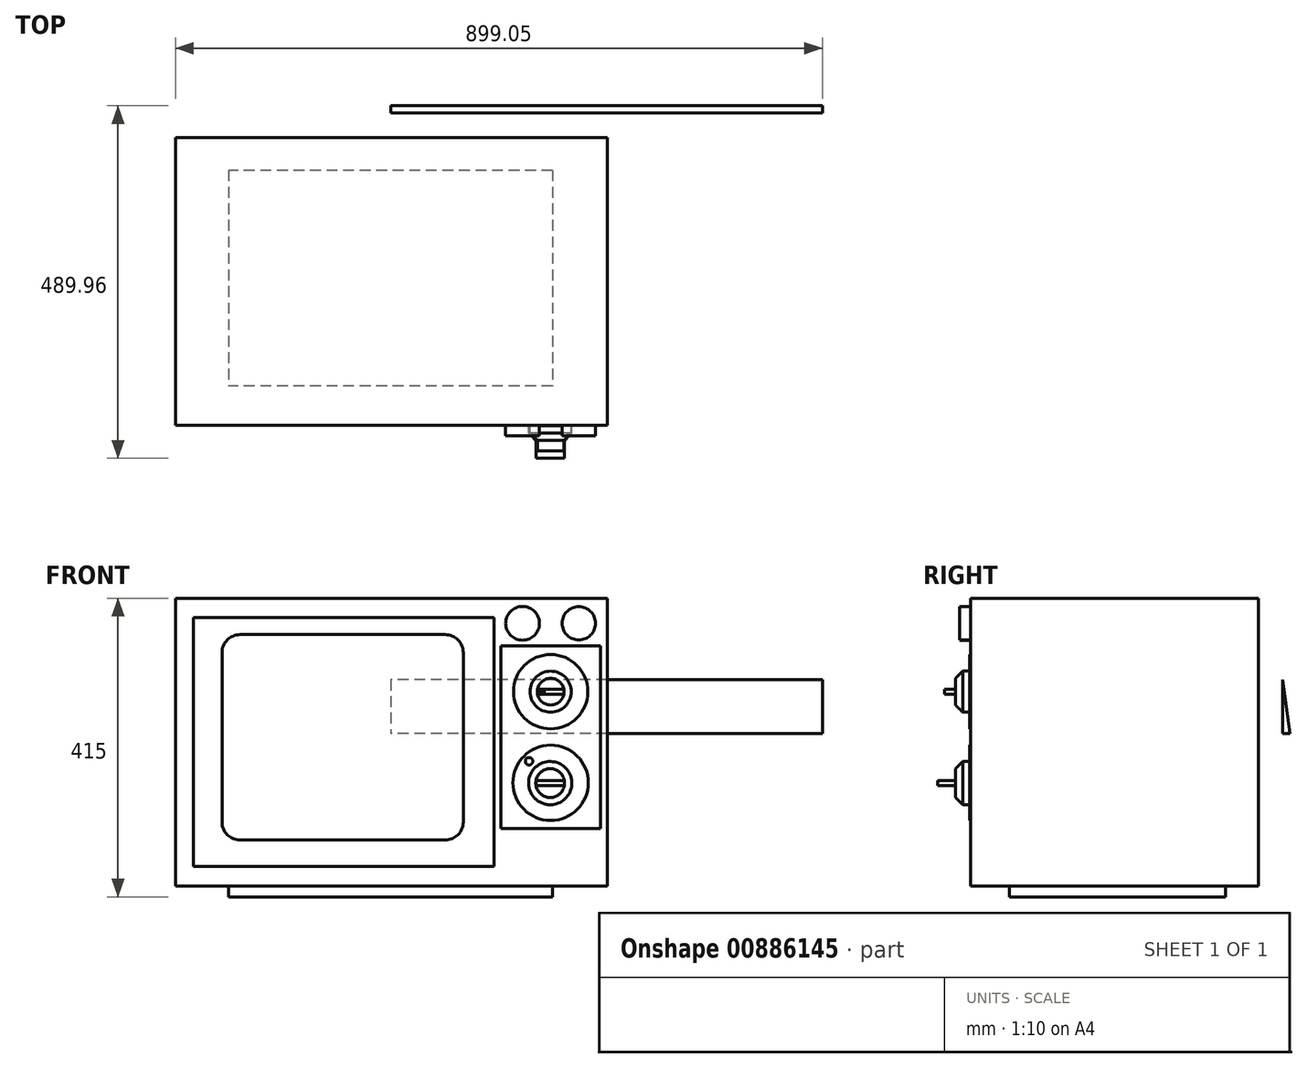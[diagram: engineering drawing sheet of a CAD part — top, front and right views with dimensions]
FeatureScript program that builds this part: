
annotation { "Feature Type Name" : "Feature", "Feature Type Description" : "" }
export const myFeature = defineFeature(function(context is Context, id is Id, definition is map)
    precondition{}
    {
        {
            var Q0;
            Q0=qCreatedBy(makeId("Front.planeOp"),FACE);
            var sketch = newSketch(context, id + "F0", { "sketchPlane" : qUnion([Q0])});
            skLineSegment(sketch, "E0.bottom", {"start": v(-299.05, 194.51) * mm, "end": v(300.95, 194.51) * mm});
            skLineSegment(sketch, "E0.top", {"start": v(-299.05, -205.49) * mm, "end": v(300.95, -205.49) * mm});
            skLineSegment(sketch, "E0.left", {"start": v(-299.05, 194.51) * mm, "end": v(-299.05, -205.49) * mm});
            skLineSegment(sketch, "E0.right", {"start": v(300.95, 194.51) * mm, "end": v(300.95, -205.49) * mm});
            skSolve(sketch);
        }
        {
            var Q0;
            Q0=makeQuery(id+"F0.imprint","IMPRINT",FACE,{"disambiguationData":[TD([[makeQuery(id+"F0.imprint","IMPRINT",EDGE,{"derivedFrom":sQuery(id+"F0.wireOp",EDGE,"E0.bottom")}),-1.0]])]});
            extrude(context, id + "F1", {"entities" : qUnion([Q0]), "depth" : 400 * mm, "offsetDistance" : 25 * mm});
        }
        {
            var Q0;
            Q0=makeQuery(id+"F1.opExtrude","CAP_FACE",FACE,{"disambiguationData":[OSD([sQuery(id+"F0.wireOp",EDGE,"E0.bottom"),sQuery(id+"F0.wireOp",EDGE,"E0.top"),sQuery(id+"F0.wireOp",EDGE,"E0.left"),sQuery(id+"F0.wireOp",EDGE,"E0.right")])],"isStart":false});
            var sketch = newSketch(context, id + "F2", { "sketchPlane" : qUnion([Q0])});
            skLineSegment(sketch, "E1.bottom", {"start": v(-274.22, 167.93) * mm, "end": v(144, 167.93) * mm});
            skLineSegment(sketch, "E1.top", {"start": v(-274.22, -178.07) * mm, "end": v(144, -178.07) * mm});
            skLineSegment(sketch, "E1.left", {"start": v(-274.22, 167.93) * mm, "end": v(-274.22, -178.07) * mm});
            skLineSegment(sketch, "E1.right", {"start": v(144, 167.93) * mm, "end": v(144, -178.07) * mm});
            skSolve(sketch);
        }
        {
            var Q0;
            Q0=makeQuery(id+"F2.imprint","IMPRINT",FACE,{"disambiguationData":[TD([[makeQuery(id+"F2.imprint","IMPRINT",EDGE,{"derivedFrom":sQuery(id+"F2.wireOp",EDGE,"E1.bottom")}),-1.0]])]});
            var sketch = newSketch(context, id + "F3", { "sketchPlane" : qUnion([Q0])});
            skSolve(sketch);
        }
        {
            var Q0;
            Q0=makeQuery(id+"F3.imprint","IMPRINT",FACE,{"disambiguationData":[TD([[makeQuery(id+"F3.imprint","IMPRINT",EDGE,{"derivedFrom":makeQuery(id+"F2.imprint","IMPRINT",EDGE,{"derivedFrom":sQuery(id+"F2.wireOp",EDGE,"E1.bottom")})}),-1.0]])]});
            extrude(context, id + "F4", {"entities" : qUnion([Q0]), "depth" : 0.01 * mm, "offsetDistance" : 25 * mm});
        }
        {
            var Q0;
            Q0=makeQuery(id+"F4.opExtrude","CAP_FACE",FACE,{"disambiguationData":[OSD([sQuery(id+"F2.wireOp",EDGE,"E1.bottom"),sQuery(id+"F2.wireOp",EDGE,"E1.top"),sQuery(id+"F2.wireOp",EDGE,"E1.left"),sQuery(id+"F2.wireOp",EDGE,"E1.right")])],"isStart":false});
            fillet(context, id + "F5", {"entities" : qUnion([Q0]), "radius" : 25 * mm, "tangentPropagation" : true, "allowEdgeOverflow" : false});
        }
        {
            var Q0;
            Q0=makeQuery(id+"F4.opExtrude","CAP_FACE",FACE,{"disambiguationData":[OSD([sQuery(id+"F2.wireOp",EDGE,"E1.bottom"),sQuery(id+"F2.wireOp",EDGE,"E1.top"),sQuery(id+"F2.wireOp",EDGE,"E1.left"),sQuery(id+"F2.wireOp",EDGE,"E1.right")])],"isStart":false});
            var sketch = newSketch(context, id + "F6", { "sketchPlane" : qUnion([Q0])});
            skLineSegment(sketch, "E2.bottom", {"start": v(-209.34, 144.13) * mm, "end": v(75.88, 144.13) * mm});
            skLineSegment(sketch, "E2.top", {"start": v(-209.34, -141.42) * mm, "end": v(75.88, -141.42) * mm});
            skLineSegment(sketch, "E2.left", {"start": v(-234.34, 119.13) * mm, "end": v(-234.34, -116.42) * mm});
            skLineSegment(sketch, "E2.right", {"start": v(100.88, 119.13) * mm, "end": v(100.88, -116.42) * mm});
            skPoint(sketch, "E3.visualSharp", {"position": v(-234.34, 144.13) * mm});
            skArc(sketch, "E3.filletArc", {"start": v(-209.34, 144.13) * mm, "mid": v(-227.02, 136.8) * mm, "end": v(-234.34, 119.13) * mm});
            skPoint(sketch, "E4.visualSharp", {"position": v(100.88, 144.13) * mm});
            skArc(sketch, "E4.filletArc", {"start": v(100.88, 119.13) * mm, "mid": v(93.55, 136.8) * mm, "end": v(75.88, 144.13) * mm});
            skPoint(sketch, "E5.visualSharp", {"position": v(100.88, -141.42) * mm});
            skArc(sketch, "E5.filletArc", {"start": v(75.88, -141.42) * mm, "mid": v(93.55, -134.1) * mm, "end": v(100.88, -116.42) * mm});
            skPoint(sketch, "E6.visualSharp", {"position": v(-234.34, -141.42) * mm});
            skArc(sketch, "E6.filletArc", {"start": v(-234.34, -116.42) * mm, "mid": v(-227.02, -134.1) * mm, "end": v(-209.34, -141.42) * mm});
            skSolve(sketch);
        }
        {
            var Q0;
            Q0=makeQuery(id+"F6.imprint","IMPRINT",FACE,{"disambiguationData":[TD([[makeQuery(id+"F6.imprint","IMPRINT",EDGE,{"derivedFrom":sQuery(id+"F6.wireOp",EDGE,"E2.bottom")}),-1.0]])]});
            extrude(context, id + "F7", {"entities" : qUnion([Q0]), "depth" : 0.01 * mm, "offsetDistance" : 25 * mm});
        }
        {
            var Q0;
            Q0=makeQuery(id+"F2.imprint","IMPRINT",FACE,{"disambiguationData":[TD([[makeQuery(id+"F2.imprint","IMPRINT",EDGE,{"derivedFrom":sQuery(id+"F2.wireOp",EDGE,"E1.bottom")}),1.0]])]});
            var sketch = newSketch(context, id + "F8", { "sketchPlane" : qUnion([Q0])});
            skCircle(sketch, "E7", {"center": v(183.33, 159.85) * mm, "radius": 23.48 * mm});
            skCircle(sketch, "E8", {"center": v(261.48, 159.85) * mm, "radius": 23.15 * mm});
            skSolve(sketch);
        }
        {
            var Q0;
            Q0 = qSketchRegion(id + "F8", true);
            extrude(context, id + "F9", {"entities" : qUnion([Q0]), "depth" : 15 * mm, "offsetDistance" : 25 * mm});
        }
        {
            var Q0;
            Q0=makeQuery(id+"F2.imprint","IMPRINT",FACE,{"disambiguationData":[TD([[makeQuery(id+"F2.imprint","IMPRINT",EDGE,{"derivedFrom":sQuery(id+"F2.wireOp",EDGE,"E1.bottom")}),1.0]])]});
            var sketch = newSketch(context, id + "F10", { "sketchPlane" : qUnion([Q0])});
            skLineSegment(sketch, "E9.bottom", {"start": v(153.12, 128.25) * mm, "end": v(291.63, 128.25) * mm});
            skLineSegment(sketch, "E9.top", {"start": v(153.12, -125.33) * mm, "end": v(291.63, -125.33) * mm});
            skLineSegment(sketch, "E9.left", {"start": v(153.12, 128.25) * mm, "end": v(153.12, -125.33) * mm});
            skLineSegment(sketch, "E9.right", {"start": v(291.63, 128.25) * mm, "end": v(291.63, -125.33) * mm});
            skSolve(sketch);
        }
        {
            var Q0;
            Q0 = qSketchRegion(id + "F10", true);
            extrude(context, id + "F11", {"entities" : qUnion([Q0]), "depth" : 0.01 * mm, "offsetDistance" : 25 * mm});
        }
        {
            var Q0;
            Q0=makeQuery(id+"F11.opExtrude","CAP_FACE",FACE,{"disambiguationData":[OSD([sQuery(id+"F10.wireOp",EDGE,"E9.bottom"),sQuery(id+"F10.wireOp",EDGE,"E9.top"),sQuery(id+"F10.wireOp",EDGE,"E9.left"),sQuery(id+"F10.wireOp",EDGE,"E9.right")])],"isStart":false});
            var sketch = newSketch(context, id + "F12", { "sketchPlane" : qUnion([Q0])});
            skCircle(sketch, "E10", {"center": v(222.37, 64.86) * mm, "radius": 51.65 * mm});
            skCircle(sketch, "E11", {"center": v(222.37, -61.94) * mm, "radius": 52.4 * mm});
            skSolve(sketch);
        }
        {
            var Q0;
            Q0=makeQuery(id+"F12.imprint","IMPRINT",FACE,{"disambiguationData":[TD([[makeQuery(id+"F12.imprint","IMPRINT",EDGE,{"derivedFrom":sQuery(id+"F12.wireOp",EDGE,"E10")}),1.0]])]});
            var Q1;
            Q1=makeQuery(id+"F12.imprint","IMPRINT",FACE,{"disambiguationData":[TD([[makeQuery(id+"F12.imprint","IMPRINT",EDGE,{"derivedFrom":sQuery(id+"F12.wireOp",EDGE,"E11")}),1.0]])]});
            extrude(context, id + "F13", {"entities" : qUnion([Q0, Q1]), "depth" : 1 * mm, "offsetDistance" : 25 * mm});
        }
        {
            var Q0;
            Q0=makeQuery(id+"F13.opExtrude","CAP_FACE",FACE,{"disambiguationData":[OSD([sQuery(id+"F12.wireOp",EDGE,"E10")])],"isStart":false});
            var sketch = newSketch(context, id + "F14", { "sketchPlane" : qUnion([Q0])});
            skCircle(sketch, "E12", {"center": v(222.37, 64.86) * mm, "radius": 28.56 * mm});
            skCircle(sketch, "E13", {"center": v(221.76, -62.3) * mm, "radius": 30.04 * mm});
            skSolve(sketch);
        }
        {
            var Q0;
            Q0 = qSketchRegion(id + "F14", true);
            extrude(context, id + "F15", {"entities" : qUnion([Q0]), "depth" : 20 * mm, "offsetDistance" : 25 * mm});
        }
        {
            var Q0;
            Q0=makeQuery(id+"F15.opExtrude","CAP_FACE",FACE,{"disambiguationData":[OSD([sQuery(id+"F14.wireOp",EDGE,"E12")])],"isStart":false});
            var Q1;
            Q1=makeQuery(id+"F15.opExtrude","CAP_FACE",FACE,{"disambiguationData":[OSD([sQuery(id+"F14.wireOp",EDGE,"E13")])],"isStart":false});
            chamfer(context, id + "F16", {"entities" : qUnion([Q0, Q1]), "width" : 10 * mm, "tangentPropagation" : true});
        }
        {
            var Q0;
            Q0=makeQuery(id+"F15.opExtrude","CAP_FACE",FACE,{"disambiguationData":[OSD([sQuery(id+"F14.wireOp",EDGE,"E12")])],"isStart":false});
            var sketch = newSketch(context, id + "F17", { "sketchPlane" : qUnion([Q0])});
            skLineSegment(sketch, "E14.bottom", {"start": v(240.6, 61.36) * mm, "end": v(204.14, 61.36) * mm});
            skLineSegment(sketch, "E14.top", {"start": v(240.6, 68.36) * mm, "end": v(204.14, 68.36) * mm});
            skLineSegment(sketch, "E14.left", {"start": v(240.6, 61.36) * mm, "end": v(240.6, 68.36) * mm});
            skLineSegment(sketch, "E14.right", {"start": v(204.14, 61.36) * mm, "end": v(204.14, 68.36) * mm});
            skPoint(sketch, "E14.middle", {"position": v(222.37, 64.86) * mm});
            skSolve(sketch);
        }
        {
            var Q0;
            Q0 = qSketchRegion(id + "F17", true);
            extrude(context, id + "F18", {"entities" : qUnion([Q0]), "depth" : 15 * mm, "offsetDistance" : 25 * mm});
        }
        {
            var Q0;
            Q0=makeQuery(id+"F15.opExtrude","CAP_FACE",FACE,{"disambiguationData":[OSD([sQuery(id+"F14.wireOp",EDGE,"E13")])],"isStart":false});
            var sketch = newSketch(context, id + "F19", { "sketchPlane" : qUnion([Q0])});
            skLineSegment(sketch, "E15.bottom", {"start": v(241.5, -65.8) * mm, "end": v(202.02, -65.8) * mm});
            skLineSegment(sketch, "E15.top", {"start": v(241.5, -58.8) * mm, "end": v(202.02, -58.8) * mm});
            skLineSegment(sketch, "E15.left", {"start": v(241.5, -65.8) * mm, "end": v(241.5, -58.8) * mm});
            skLineSegment(sketch, "E15.right", {"start": v(202.02, -65.8) * mm, "end": v(202.02, -58.8) * mm});
            skPoint(sketch, "E15.middle", {"position": v(221.76, -62.3) * mm});
            skSolve(sketch);
        }
        {
            var Q0;
            Q0 = qSketchRegion(id + "F19", true);
            extrude(context, id + "F20", {"entities" : qUnion([Q0]), "operationType" : NewBodyOperationType.ADD, "depth" : 25 * mm, "offsetDistance" : 25 * mm});
        }
        {
            var Q0;
            Q0=makeQuery(id+"F1.opExtrude","SWEPT_FACE",FACE,{"disambiguationData":[OSD([sQuery(id+"F0.wireOp",EDGE,"E0.top")])]});
            var sketch = newSketch(context, id + "F21", { "sketchPlane" : qUnion([Q0])});
            skLineSegment(sketch, "E16.bottom", {"start": v(225, 45.8) * mm, "end": v(-225, 45.8) * mm});
            skLineSegment(sketch, "E16.top", {"start": v(225, 345.8) * mm, "end": v(-225, 345.8) * mm});
            skLineSegment(sketch, "E16.left", {"start": v(225, 45.8) * mm, "end": v(225, 345.8) * mm});
            skLineSegment(sketch, "E16.right", {"start": v(-225, 45.8) * mm, "end": v(-225, 345.8) * mm});
            skPoint(sketch, "E16.middle", {"position": v(0, 195.8) * mm});
            skSolve(sketch);
        }
        {
            var Q0;
            Q0 = qSketchRegion(id + "F21", true);
            extrude(context, id + "F22", {"entities" : qUnion([Q0]), "depth" : 15 * mm, "offsetDistance" : 25 * mm});
        }
        {
            var Q0;
            Q0=makeQuery(id+"F13.opExtrude","CAP_FACE",FACE,{"disambiguationData":[OSD([sQuery(id+"F12.wireOp",EDGE,"E11")])],"isStart":false});
            var sketch = newSketch(context, id + "F23", { "sketchPlane" : qUnion([Q0])});
            skPoint(sketch, "E17", {"position": v(222.37, -61.94) * mm});
            skCircle(sketch, "E18", {"center": v(192.38, -31.94) * mm, "radius": 5.2 * mm});
            skSolve(sketch);
        }
        {
            var Q0;
            Q0=makeQuery(id+"F23.imprint","IMPRINT",FACE,{"disambiguationData":[TD([[makeQuery(id+"F23.imprint","IMPRINT",EDGE,{"derivedFrom":sQuery(id+"F23.wireOp",EDGE,"jFTy3HLy-dIud-ZenL-b3eB-yhUInUCiy9Uc")}),1.0]])]});
            var Q1;
            Q1=makeQuery(id+"F23.imprint","IMPRINT",FACE,{"disambiguationData":[TD([[makeQuery(id+"F23.imprint","IMPRINT",EDGE,{"derivedFrom":sQuery(id+"F23.wireOp",EDGE,"QcOYSMLE-XDyg-PND2-6kcq-p4WEsHTPSeWB")}),1.0]])]});
            var Q2;
            Q2=makeQuery(id+"F23.imprint","IMPRINT",FACE,{"disambiguationData":[TD([[makeQuery(id+"F23.imprint","IMPRINT",EDGE,{"derivedFrom":sQuery(id+"F23.wireOp",EDGE,"uuDVGhji-J2iJ-84Kr-mtZB-Ht9td2afYEIX")}),1.0]])]});
            var Q3;
            Q3=makeQuery(id+"F23.imprint","IMPRINT",FACE,{"disambiguationData":[TD([[makeQuery(id+"F23.imprint","IMPRINT",EDGE,{"derivedFrom":sQuery(id+"F23.wireOp",EDGE,"E18")}),1.0]])]});
            var Q4;
            Q4=makeQuery(id+"F23.imprint","IMPRINT",FACE,{"disambiguationData":[TD([[makeQuery(id+"F23.imprint","IMPRINT",EDGE,{"derivedFrom":sQuery(id+"F23.wireOp",EDGE,"LvY0InTs-vciN-NS8o-lJkW-nBjZa8jqqQHf")}),1.0]])]});
            var Q5;
            Q5=makeQuery(id+"F23.imprint","IMPRINT",FACE,{"disambiguationData":[TD([[makeQuery(id+"F23.imprint","IMPRINT",EDGE,{"derivedFrom":sQuery(id+"F23.wireOp",EDGE,"Qzo9KO9w-CmhF-6eXv-hFlw-EyqTfP6HEGoB")}),1.0]])]});
            var Q6;
            Q6=makeQuery(id+"F23.imprint","IMPRINT",FACE,{"disambiguationData":[TD([[makeQuery(id+"F23.imprint","IMPRINT",EDGE,{"derivedFrom":sQuery(id+"F23.wireOp",EDGE,"llRZ0wBM-Syag-fE8T-zaAk-blLDZ9ETd807")}),1.0]])]});
            var Q7;
            Q7=makeQuery(id+"F23.imprint","IMPRINT",FACE,{"disambiguationData":[TD([[makeQuery(id+"F23.imprint","IMPRINT",EDGE,{"derivedFrom":sQuery(id+"F23.wireOp",EDGE,"deQryJkM-4fHw-CP0u-ul9e-cYhTYZMcB6DS")}),1.0]])]});
            var Q8;
            Q8=makeQuery(id+"F23.imprint","IMPRINT",FACE,{"disambiguationData":[TD([[makeQuery(id+"F23.imprint","IMPRINT",EDGE,{"derivedFrom":sQuery(id+"F23.wireOp",EDGE,"w7Ipdqzw-WEb8-gp5m-Ikwh-9nXrJSbfsVlL")}),1.0]])]});
            var Q9;
            Q9=makeQuery(id+"F23.imprint","IMPRINT",FACE,{"disambiguationData":[TD([[makeQuery(id+"F23.imprint","IMPRINT",EDGE,{"derivedFrom":sQuery(id+"F23.wireOp",EDGE,"DbhkNCz8-OPGq-1Fgp-E6qm-TmXsteiqtAnb")}),1.0]])]});
            var Q10;
            Q10=makeQuery(id+"F23.imprint","IMPRINT",FACE,{"disambiguationData":[TD([[makeQuery(id+"F23.imprint","IMPRINT",EDGE,{"derivedFrom":sQuery(id+"F23.wireOp",EDGE,"UCcNfzIB-eb0M-zC80-nXF0-guQ6JpqgJsuD")}),1.0]])]});
            var Q11;
            Q11=makeQuery(id+"F23.imprint","IMPRINT",FACE,{"disambiguationData":[TD([[makeQuery(id+"F23.imprint","IMPRINT",EDGE,{"derivedFrom":sQuery(id+"F23.wireOp",EDGE,"ZEoHDBkx-05wF-JX6h-3mDG-D2dnclyBwI5X")}),1.0]])]});
            var Q12;
            Q12=makeQuery(id+"F23.imprint","IMPRINT",FACE,{"disambiguationData":[TD([[makeQuery(id+"F23.imprint","IMPRINT",EDGE,{"derivedFrom":sQuery(id+"F23.wireOp",EDGE,"LCFa3XmW-8JGb-WoMI-bgxg-AmZSnI9t5JsV")}),1.0]])]});
            var Q13;
            Q13=makeQuery(id+"F23.imprint","IMPRINT",FACE,{"disambiguationData":[TD([[makeQuery(id+"F23.imprint","IMPRINT",EDGE,{"derivedFrom":sQuery(id+"F23.wireOp",EDGE,"6qCvgCml-s3bJ-azFm-QWmR-aGI0sdzBvxI3")}),1.0]])]});
            var Q14;
            Q14=makeQuery(id+"F23.imprint","IMPRINT",FACE,{"disambiguationData":[TD([[makeQuery(id+"F23.imprint","IMPRINT",EDGE,{"derivedFrom":sQuery(id+"F23.wireOp",EDGE,"P2OSG97K-7TvJ-fS5s-33Ce-i53BDxxE9sIs")}),1.0]])]});
            var Q15;
            Q15=makeQuery(id+"F23.imprint","IMPRINT",FACE,{"disambiguationData":[TD([[makeQuery(id+"F23.imprint","IMPRINT",EDGE,{"derivedFrom":sQuery(id+"F23.wireOp",EDGE,"4JE0RNnv-zySG-nhiA-yIyW-ZmG5gZb6r83r")}),1.0]])]});
            extrude(context, id + "F24", {"entities" : qUnion([Q0, Q1, Q2, Q3, Q4, Q5, Q6, Q7, Q8, Q9, Q10, Q11, Q12, Q13, Q14, Q15]), "depth" : 0.01 * mm, "offsetDistance" : 25 * mm});
        }
        {
            var Q0;
            Q0=makeQuery(id+"F18.opExtrude","CAP_FACE",FACE,{"disambiguationData":[OSD([sQuery(id+"F17.wireOp",EDGE,"E14.bottom"),sQuery(id+"F17.wireOp",EDGE,"E14.top"),sQuery(id+"F17.wireOp",EDGE,"E14.left"),sQuery(id+"F17.wireOp",EDGE,"E14.right")])],"isStart":false});
            var sketch = newSketch(context, id + "F25", { "sketchPlane" : qUnion([Q0])});
            skLineSegment(sketch, "E19", {"start": v(213.26, 64.86) * mm, "end": v(213.26, 68.36) * mm, "construction": true});
            skLineSegment(sketch, "E20", {"start": v(213.26, 68.36) * mm, "end": v(213.26, 64.86) * mm, "construction": true});
            skLineSegment(sketch, "E21", {"start": v(213.26, 61.36) * mm, "end": v(213.26, 64.86) * mm, "construction": true});
            skLineSegment(sketch, "E22", {"start": v(213.26, 66.6) * mm, "end": v(206.05, 64.86) * mm});
            skLineSegment(sketch, "E23", {"start": v(206.05, 64.86) * mm, "end": v(213.26, 63.1) * mm});
            skLineSegment(sketch, "E24", {"start": v(213.26, 63.1) * mm, "end": v(213.26, 66.6) * mm});
            skSolve(sketch);
        }
        {
            var Q0;
            Q0=makeQuery(id+"F25.imprint","IMPRINT",FACE,{"disambiguationData":[TD([[makeQuery(id+"F25.imprint","IMPRINT",EDGE,{"derivedFrom":sQuery(id+"F25.wireOp",EDGE,"E22")}),1.0]])]});
            extrude(context, id + "F26", {"entities" : qUnion([Q0]), "depth" : 0.01 * mm, "offsetDistance" : 25 * mm});
        }
        {
            var Q0;
            Q0=qCreatedBy(makeId("Right.planeOp"),FACE);
            var sketch = newSketch(context, id + "F27", { "sketchPlane" : qUnion([Q0])});
            skLineSegment(sketch, "E25.left", {"start": v(33.95, 81.52) * mm, "end": v(33.95, 6.52) * mm});
            skLineSegment(sketch, "E26", {"start": v(33.95, 6.52) * mm, "end": v(43.95, 6.52) * mm});
            skLineSegment(sketch, "E27", {"start": v(33.95, 81.52) * mm, "end": v(43.95, 6.52) * mm});
            skPoint(sketch, "E25.bottom.end.orphan", {"position": v(43.95, 231.52) * mm});
            skPoint(sketch, "E28.orphan", {"position": v(33.95, 231.52) * mm});
            skPoint(sketch, "E29.end.orphan", {"position": v(43.95, 81.52) * mm});
            skPoint(sketch, "E25.top.end.orphan", {"position": v(43.95, -68.48) * mm});
            skPoint(sketch, "E25.top.start.orphan", {"position": v(33.95, -68.48) * mm});
            skSolve(sketch);
        }
        {
            var Q0;
            Q0 = qSketchRegion(id + "F27", true);
            extrude(context, id + "F28", {"entities" : qUnion([Q0]), "depth" : 600 * mm, "offsetDistance" : 25 * mm});
        }
    });
